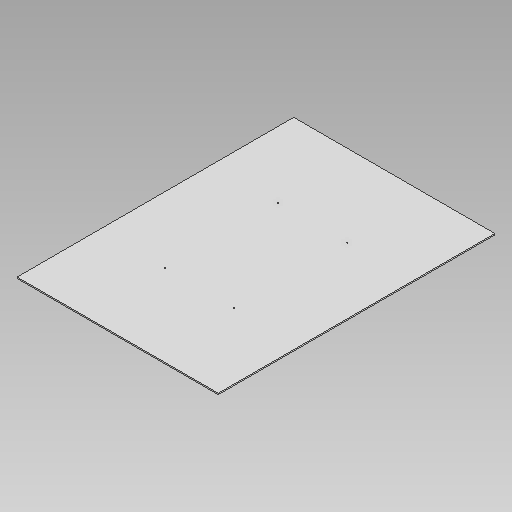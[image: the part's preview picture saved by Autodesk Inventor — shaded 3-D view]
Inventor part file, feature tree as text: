
AUTODESK INVENTOR PART (.ipt)
format: ipt  version: 2021 (Build 250183000, 183)  size: 121,344 bytes
history: native  units: mm
features: sketch x2, extrude x1, hole x1
ambient origin geometry x8: Origin, YZ Plane, XZ Plane, XY Plane, X Axis, Y Axis, Z Axis, Center Point
bodies: Solid1 (feature_tree)
feature tree (4):
  extrude  "base"  Depth=2200.0mm
  hole  "mountHoles"  [1 undecoded]
  sketch  "Sketch1"  dims[d0=1100.0mm d1=2200.0mm]
  sketch  "Sketch2"  dims[d2=1600.0mm d3=800.0mm d4=10.0mm d5=0.0mm d10=900.0mm d11=900.0mm d12=550.0mm d13=550.0mm d14=275.0mm d15=275.0mm d16=450.0mm d17=450.0mm d18=10.0mm d19=8.0mm d20=4.0mm d21=2.0mm d22=90.0deg d23=8.0mm d24=20.594885mm]
note: 1 required parameter value undecoded (feature->parameter linkage not recoverable at this tier; creation-order binding heuristic only, values carry confidence <= 0.55)
